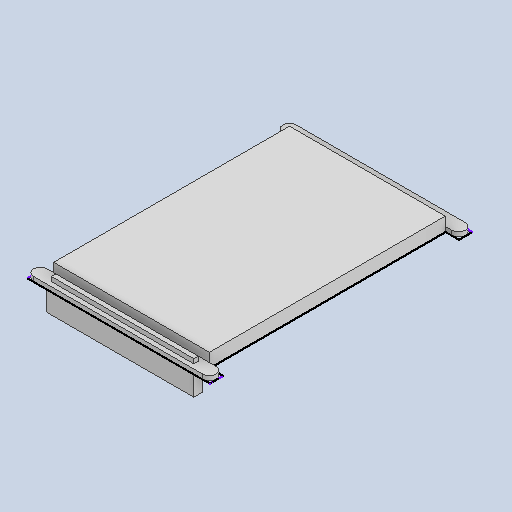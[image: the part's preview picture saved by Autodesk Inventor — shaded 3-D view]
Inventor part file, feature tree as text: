
AUTODESK INVENTOR PART (.ipt)
format: ipt  version: 2023 (Build 270158000, 158)  size: 286,208 bytes
history: native  units: in
note: dims shown in document units (in); Inventor stores cm internally (conversion verified against a paired STEP export)
features: extrude x5, sketch x1, fillet x1
ambient origin geometry x8: Origin, YZ Plane, XZ Plane, XY Plane, X Axis, Y Axis, Z Axis, Center Point
bodies: Solid1 (feature_tree)
feature tree (7):
  sketch  "Sketch1"  dims[d0=2.1875in d1=3.3125in d2=2.1875in d4=2.1875in d7=0.1875in d8=0.1875in d9=0.1875in d10=2.0in d12=0.0625in d13=0.0625in d14=0.0938in d15=0.0312in d16=0.1875in d17=0.0in d18=0.0625in d19=0.0in d20=0.0625in d21=0.0in d22=0.125in d23=0.0in d24=0.3125in d25=0.0in d26=0.0938in]
  extrude  "Extrusion1"  Depth=3.3125in
  extrude  "Extrusion2"  Depth=2.1875in
  extrude  "Extrusion3"  Depth=2.1875in
  extrude  "Extrusion4"  Depth=0.1875in
  extrude  "Extrusion5"  Depth=0.1875in
  fillet  "Fillet1"  Radius=0.1875in
